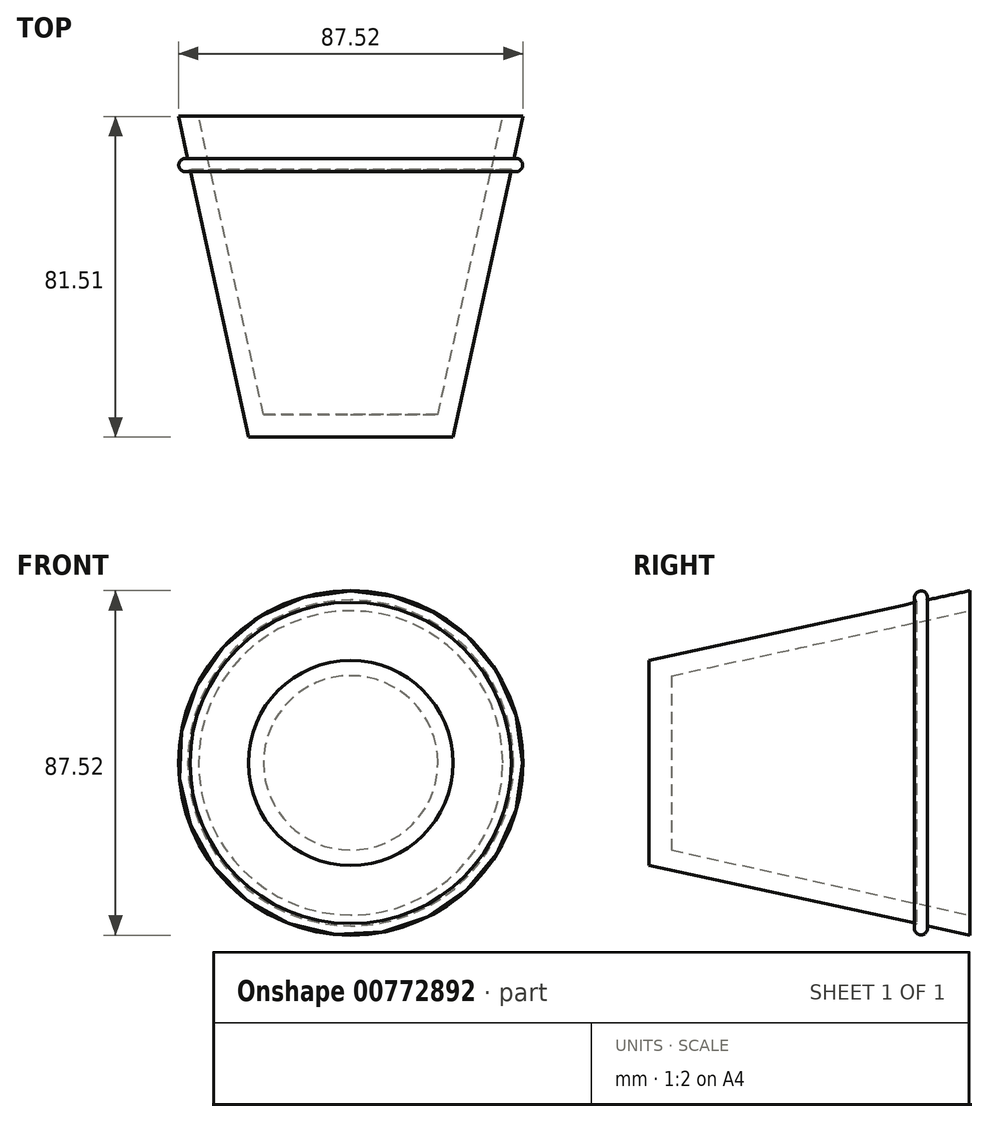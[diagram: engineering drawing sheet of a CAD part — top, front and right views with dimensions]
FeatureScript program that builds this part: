
annotation { "Feature Type Name" : "Feature", "Feature Type Description" : "" }
export const myFeature = defineFeature(function(context is Context, id is Id, definition is map)
    precondition{}
    {
        {
            var Q0;
            Q0=qCreatedBy(makeId("Top.planeOp"),FACE);
            var sketch = newSketch(context, id + "F0", { "sketchPlane" : qUnion([Q0])});
            skLineSegment(sketch, "E0", {"start": v(-43.76, 39.55) * mm, "end": v(-26.02, -41.96) * mm});
            skLineSegment(sketch, "E1", {"start": v(-26.02, -41.96) * mm, "end": v(0, -41.96) * mm});
            skLineSegment(sketch, "E2", {"start": v(-38.65, 39.55) * mm, "end": v(-22.15, -36.23) * mm});
            skLineSegment(sketch, "E3", {"start": v(-22.15, -36.23) * mm, "end": v(0, -36.23) * mm});
            skLineSegment(sketch, "E4", {"start": v(0, -36.23) * mm, "end": v(0, -41.96) * mm});
            skArc(sketch, "E5", {"start": v(-41.4, 28.72) * mm, "mid": v(-43.65, 26.8) * mm, "end": v(-40.82, 26) * mm});
            skArc(sketch, "E6.0.1.0", {"start": v(-41.4, 25.34) * mm, "mid": v(-43.65, 23.43) * mm, "end": v(-40.82, 22.63) * mm});
            skArc(sketch, "E6.0.2.0", {"start": v(-41.4, 21.96) * mm, "mid": v(-43.65, 20.05) * mm, "end": v(-40.82, 19.25) * mm});
            skArc(sketch, "E6.0.3.0", {"start": v(-41.4, 18.58) * mm, "mid": v(-43.65, 16.67) * mm, "end": v(-40.82, 15.87) * mm});
            skArc(sketch, "E6.0.4.0", {"start": v(-41.4, 15.2) * mm, "mid": v(-43.65, 13.3) * mm, "end": v(-40.82, 12.5) * mm});
            skArc(sketch, "E6.0.5.0", {"start": v(-41.4, 11.82) * mm, "mid": v(-43.65, 9.92) * mm, "end": v(-40.82, 9.11) * mm});
            skArc(sketch, "E6.1.1.0", {"start": v(-41.4, 25.34) * mm, "mid": v(-43.65, 23.43) * mm, "end": v(-40.82, 22.63) * mm});
            skArc(sketch, "E6.1.2.0", {"start": v(-41.4, 21.96) * mm, "mid": v(-43.65, 20.05) * mm, "end": v(-40.82, 19.25) * mm});
            skArc(sketch, "E6.1.3.0", {"start": v(-41.4, 18.58) * mm, "mid": v(-43.65, 16.67) * mm, "end": v(-40.82, 15.87) * mm});
            skArc(sketch, "E6.1.4.0", {"start": v(-41.4, 15.2) * mm, "mid": v(-43.65, 13.3) * mm, "end": v(-40.82, 12.5) * mm});
            skArc(sketch, "E6.1.5.0", {"start": v(-41.4, 11.82) * mm, "mid": v(-43.65, 9.92) * mm, "end": v(-40.82, 9.11) * mm});
            skArc(sketch, "E6.2.1.0", {"start": v(-41.4, 25.34) * mm, "mid": v(-43.65, 23.43) * mm, "end": v(-40.82, 22.63) * mm});
            skArc(sketch, "E6.2.2.0", {"start": v(-41.4, 21.96) * mm, "mid": v(-43.65, 20.05) * mm, "end": v(-40.82, 19.25) * mm});
            skArc(sketch, "E6.2.3.0", {"start": v(-41.4, 18.58) * mm, "mid": v(-43.65, 16.67) * mm, "end": v(-40.82, 15.87) * mm});
            skArc(sketch, "E6.2.4.0", {"start": v(-41.4, 15.2) * mm, "mid": v(-43.65, 13.3) * mm, "end": v(-40.82, 12.5) * mm});
            skArc(sketch, "E6.2.5.0", {"start": v(-41.4, 11.82) * mm, "mid": v(-43.65, 9.92) * mm, "end": v(-40.82, 9.11) * mm});
            skLineSegment(sketch, "E6.direction1", {"start": v(-42.02, 27.16) * mm, "end": v(-42.02, 27.16) * mm});
            skLineSegment(sketch, "E6.direction2", {"start": v(-42.02, 27.16) * mm, "end": v(-42.02, 23.78) * mm, "construction": true});
            skLineSegment(sketch, "E7", {"start": v(-43.76, 39.55) * mm, "end": v(-38.65, 39.55) * mm});
            skLineSegment(sketch, "E8", {"start": v(-41.4, 25.34) * mm, "end": v(-40.82, 9.11) * mm});
            skLineSegment(sketch, "E9", {"start": v(-41.4, 21.96) * mm, "end": v(-41.4, 11.82) * mm});
            skSolve(sketch);
        }
        {
            var Q0;
            {var subQ0=sQuery(id+"F0.wireOp",EDGE,"E1");Q0=makeQuery(id+"F0.imprint","IMPRINT",FACE,{"disambiguationData":[TD([[makeQuery(id+"F0.imprint","IMPRINT",EDGE,{"derivedFrom":subQ0}),1.0]])]});}
            var Q1;
            {var subQ5=sQuery(id+"F0.wireOp",EDGE,"E6.2.5.0");Q1=makeQuery(id+"F0.imprint","IMPRINT",FACE,{"disambiguationData":[TD([[makeQuery(id+"F0.imprint","IMPRINT",EDGE,{"derivedFrom":subQ5}),1.0]])]});}
            var Q2;
            {var subQ0=sQuery(id+"F0.wireOp",EDGE,"E9");var subQ1=sQuery(id+"F0.wireOp",EDGE,"E6.2.4.0");var subQ2=makeQuery(id+"F0.imprint","INTERSECT",VERTEX,{"disambiguationData":[OD(0.0)],"derivedFrom":[subQ1,subQ0]});Q2=makeQuery(id+"F0.imprint","IMPRINT",FACE,{"disambiguationData":[TD([[makeQuery(id+"F0.imprint","IMPRINT",EDGE,{"disambiguationData":[TD([[subQ2,-1.0]])],"derivedFrom":subQ1}),1.0]])]});}
            var Q3;
            {var subQ0=sQuery(id+"F0.wireOp",EDGE,"E9");var subQ1=sQuery(id+"F0.wireOp",EDGE,"E6.2.3.0");var subQ2=makeQuery(id+"F0.imprint","INTERSECT",VERTEX,{"disambiguationData":[OD(0.0)],"derivedFrom":[subQ1,subQ0]});Q3=makeQuery(id+"F0.imprint","IMPRINT",FACE,{"disambiguationData":[TD([[makeQuery(id+"F0.imprint","IMPRINT",EDGE,{"disambiguationData":[TD([[subQ2,-1.0]])],"derivedFrom":subQ1}),1.0]])]});}
            var Q4;
            {var subQ0=sQuery(id+"F0.wireOp",EDGE,"E8");var subQ1=sQuery(id+"F0.wireOp",EDGE,"E6.2.1.0");var subQ2=makeQuery(id+"F0.imprint","INTERSECT",VERTEX,{"disambiguationData":[OD(0.0)],"derivedFrom":[subQ1,subQ0]});Q4=makeQuery(id+"F0.imprint","IMPRINT",FACE,{"disambiguationData":[TD([[makeQuery(id+"F0.imprint","IMPRINT",EDGE,{"disambiguationData":[TD([[subQ2,-1.0]])],"derivedFrom":subQ1}),1.0]])]});}
            var Q5;
            {var subQ0=sQuery(id+"F0.wireOp",EDGE,"E5");Q5=makeQuery(id+"F0.imprint","IMPRINT",FACE,{"disambiguationData":[TD([[makeQuery(id+"F0.imprint","IMPRINT",EDGE,{"derivedFrom":subQ0}),1.0]])]});}
            var Q6;
            {var subQ3=sQuery(id+"F0.wireOp",EDGE,"E6.2.3.0");var subQ5=sQuery(id+"F0.wireOp",EDGE,"E8");var subQ6=makeQuery(id+"F0.imprint","INTERSECT",VERTEX,{"derivedFrom":[subQ3,subQ5]});Q6=makeQuery(id+"F0.imprint","IMPRINT",FACE,{"disambiguationData":[TD([[makeQuery(id+"F0.imprint","IMPRINT",EDGE,{"disambiguationData":[TD([[subQ6,1.0]])],"derivedFrom":subQ3}),-1.0]])]});}
            var Q7;
            {var subQ0=sQuery(id+"F0.wireOp",EDGE,"E8");var subQ1=sQuery(id+"F0.wireOp",EDGE,"E6.2.2.0");var subQ2=makeQuery(id+"F0.imprint","INTERSECT",VERTEX,{"derivedFrom":[subQ1,subQ0]});Q7=makeQuery(id+"F0.imprint","IMPRINT",FACE,{"disambiguationData":[TD([[makeQuery(id+"F0.imprint","IMPRINT",EDGE,{"disambiguationData":[TD([[subQ2,1.0]])],"derivedFrom":subQ1}),-1.0]])]});}
            var Q8;
            {var subQ0=sQuery(id+"F0.wireOp",EDGE,"E9");var subQ1=sQuery(id+"F0.wireOp",EDGE,"E6.2.2.0");var subQ2=makeQuery(id+"F0.imprint","INTERSECT",VERTEX,{"disambiguationData":[OD(0.0)],"derivedFrom":[subQ1,subQ0]});Q8=makeQuery(id+"F0.imprint","IMPRINT",FACE,{"disambiguationData":[TD([[makeQuery(id+"F0.imprint","IMPRINT",EDGE,{"disambiguationData":[TD([[subQ2,-1.0]])],"derivedFrom":subQ1}),1.0]])]});}
            var Q9;
            Q9=sQuery(id+"F0.wireOp",EDGE,"E4");
            revolve(context, id + "F1", {"surfaceOperationType" : NewSurfaceOperationType.NEW, "entities" : qUnion([Q0, Q1, Q2, Q3, Q4, Q5, Q6, Q7, Q8]), "axis" : qUnion([Q9]), "revolveType" : RevolveType.FULL});
        }
    });
